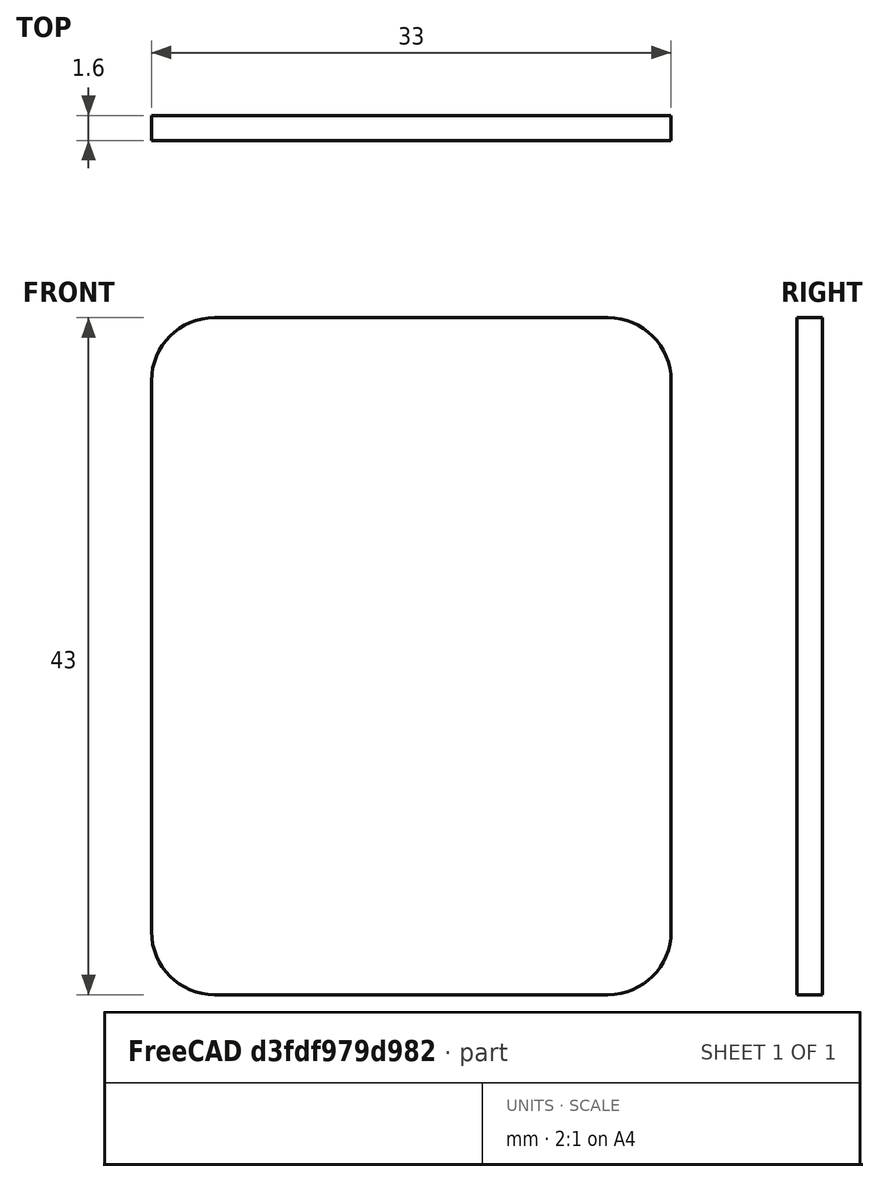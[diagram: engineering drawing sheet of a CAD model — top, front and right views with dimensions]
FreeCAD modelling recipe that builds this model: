
FCSTD DOCUMENT  (FreeCAD 0.20R29603 (Git))
Label: Right Throttle Board rev1
License: All rights reserved
LicenseURL: http://en.wikipedia.org/wiki/All_rights_reserved
objects: Sketcher::SketchObject×1, PartDesign::Pad×1, PartDesign::Body×1
note: 4 computed .brp shape members not serialized (recipe doc carries the construction recipe); baked Part::Feature solids carry a one-line shape summary decoded from their .brp

FEATURE [Sketcher::SketchObject] Sketch
  FullyConstrained = true
  MapMode = 5
  Placement = pos=(0,0,0) rot=(1,0,0;1.5708rad)
  Support = -> [XZ_Plane]
  sketch-geometry (8):
    g0: LineSegment StartX=-12.5 StartY=21.5 StartZ=0 EndX=12.5 EndY=21.5 EndZ=0
    g1: LineSegment StartX=16.5 StartY=17.5 StartZ=0 EndX=16.5 EndY=-17.5 EndZ=0
    g2: LineSegment StartX=12.5 StartY=-21.5 StartZ=0 EndX=-12.5 EndY=-21.5 EndZ=0
    g3: LineSegment StartX=-16.5 StartY=-17.5 StartZ=0 EndX=-16.5 EndY=17.5 EndZ=0
    g4: ArcOfCircle CenterX=-12.5 CenterY=17.5 CenterZ=0 NormalX=0 NormalY=0 NormalZ=1 AngleXU=0 Radius=4 StartAngle=1.5708 EndAngle=3.14159
    g5: ArcOfCircle CenterX=12.5 CenterY=17.5 CenterZ=0 NormalX=0 NormalY=0 NormalZ=1 AngleXU=0 Radius=4 StartAngle=-9e-16 EndAngle=1.5708
    g6: ArcOfCircle CenterX=-12.5 CenterY=-17.5 CenterZ=0 NormalX=0 NormalY=0 NormalZ=1 AngleXU=0 Radius=4 StartAngle=3.14159 EndAngle=4.71239
    g7: ArcOfCircle CenterX=12.5 CenterY=-17.5 CenterZ=0 NormalX=0 NormalY=0 NormalZ=1 AngleXU=0 Radius=4 StartAngle=4.71239 EndAngle=6.28319
  constraints (18):
    c: Horizontal(g0)
    c: Horizontal(g2)
    c: Vertical(g3)
    c: Tangent(g0,g4) = 1.5708
    c: Tangent(g3,g4) = 1.5708
    c: Radius(g4) = 4
    c: Tangent(g0,g5) = 1.5708
    c: Tangent(g1,g5) = 1.5708
    c: Tangent(g2,g6) = 1.5708
    c: Tangent(g3,g6) = 1.5708
    c: Radius(g6) = 4
    c: Tangent(g1,g7) = 1.5708
    c: Tangent(g2,g7) = 1.5708
    c: Radius(g7) = 4
    c: Symmetric(g3,g1,g-2)
    c: DistanceX(g0,g0) = 25
    c: DistanceY(g1,g1) = 35
    c: Symmetric(g1,g1,g-1)
FEATURE [PartDesign::Pad] Pad
  Direction = (0,-1,2e-16)
  Length = 1.6
  Length2 = 10
  Placement = pos=(0,0,0) rot=(1,0,0;1.5708rad)
  Profile = -> Sketch
  ReferenceAxis = -> Sketch [N_Axis]
  Type = 0
FEATURE [PartDesign::Body] Body
  Group = -> [Sketch,Pad]
  Origin = -> Origin
  Tip = -> Pad
